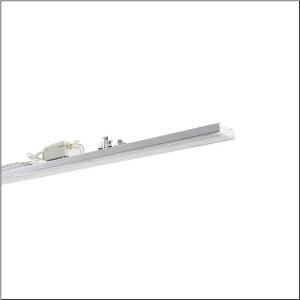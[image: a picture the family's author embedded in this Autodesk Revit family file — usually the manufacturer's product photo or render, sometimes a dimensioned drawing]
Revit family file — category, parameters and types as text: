
# Revit family: licross_11_recessed_mo_51tl19cn485g
name_source: partatom
category: Lighting Fixtures
units: mm (PartAtom-declared; Revit-internal decimal feet)

## family parameters
Cut with Voids When Loaded = No
Host = Face
Light Source = No
Part Type = Normal
Room Calculation Point = No
Round Connector Dimension = Use Diameter
Shared = No

## types (1)
- --- (1 x LED, 8920 lm, 49.3 W, 4000K)
    Apparent Load = 49 VA
    CIE Flux Codes = 55 90 98 100 100
    Color Rendering = 80
    Color Temperature = 4000K
    Default Elevation = 1800 mm
    Description = Licross 11 Recessed MO, luminaire insert, of sheet steel, coil coated, white, length: 1.500mm, width: 66mm, height: 67mm, LED rated luminous flux: 8.920lm, light colour: 840, SDCM (Standard Deviation of Colour Matching)MacAdam ≤ 2 SDCM (initial), control gear: ON/OFF Multilumen, CLOi, with plug, 3-pole, with phase selection, mains connection: 220..240V, AC, 50/60Hz, start of lifetime: 49W, end of service life: 55W, internal wiring halogen-free, primary light control with lens, of plastic, primary optical cover: cover, of PMMA, light emission: direct distribution, primary light characteristic: double asymmetric, protection rating (complete): IP40, insulation class (complete): insulation class I (protective earthing), certification: CE, ENEC, VDE, UKCA, protection symbol: D if used in an environment without relevant dust loads with corresponding accessories, impact resistance: IK06, permissible ambient temperature for indoor applications: -35..+40°C, corresponds to IFS (International Featured Standards) requirements for safety and quality in the food industry, reducing of maximum allowable ambient temperature of 5°C with ceiling mounting, LABS conformity tested according to VDMA 24364:2018-05, The light source and the operating device comply with the requirements of the Ecodesign Regulation (EU) 2019/2020 and are replaceable in accordance with this regulation, packaging unit: 1 piece
    Height = 58 mm
    Lamp = 1 x LED
    Lamp Light Flux = 8920 lm
    Lamp Power = 49.3 W
    Lamp count = 1
    Length = 1500 mm
    Luminous efficacy = 181 lm/W
    Manufacturer = Siteco
    ModVariant = No
    Model = 51TL19CN485G
    Mounting Place = Ceiling
    Mounting Type = Pendant
    Number of Poles = 1
    OnlyDefault = Yes
    Power Factor = 1
    Product Name = Licross 11 Recessed MO
    Product group = luminaire insert | ceiling pendant
    ProductGroupID = 901
    Protection Class = Protection class I
    Protection Degree = IP 40
    RLX_Detail_Level = 1
    RLX_Emergency_Light_Flux = 0 lm
    RLX_Emergency_Type = 0
    RLX_Emergency_Type_DB = No
    RlxData = <blob elided: 22573 chars, md5=a0675106>
    Socket = socket
    Standby Power = 0 W
    System Light Flux = 8920 lm
    System Power = 49 W
    Type Comments = factory setting: luminous flux: 100 % | (A | C | E) | 113 mA
    Type Image = l_1296930.jpg
    URL = http://relux.com
    VarID = @adj_000617
    Voltage = 0 V
    Weight = 0.00 kg
    Width = 66 mm

## geometry (parser evidence)
native form markers: Blend x4, Sweep x11
no freeform markers — native parametric forms only
